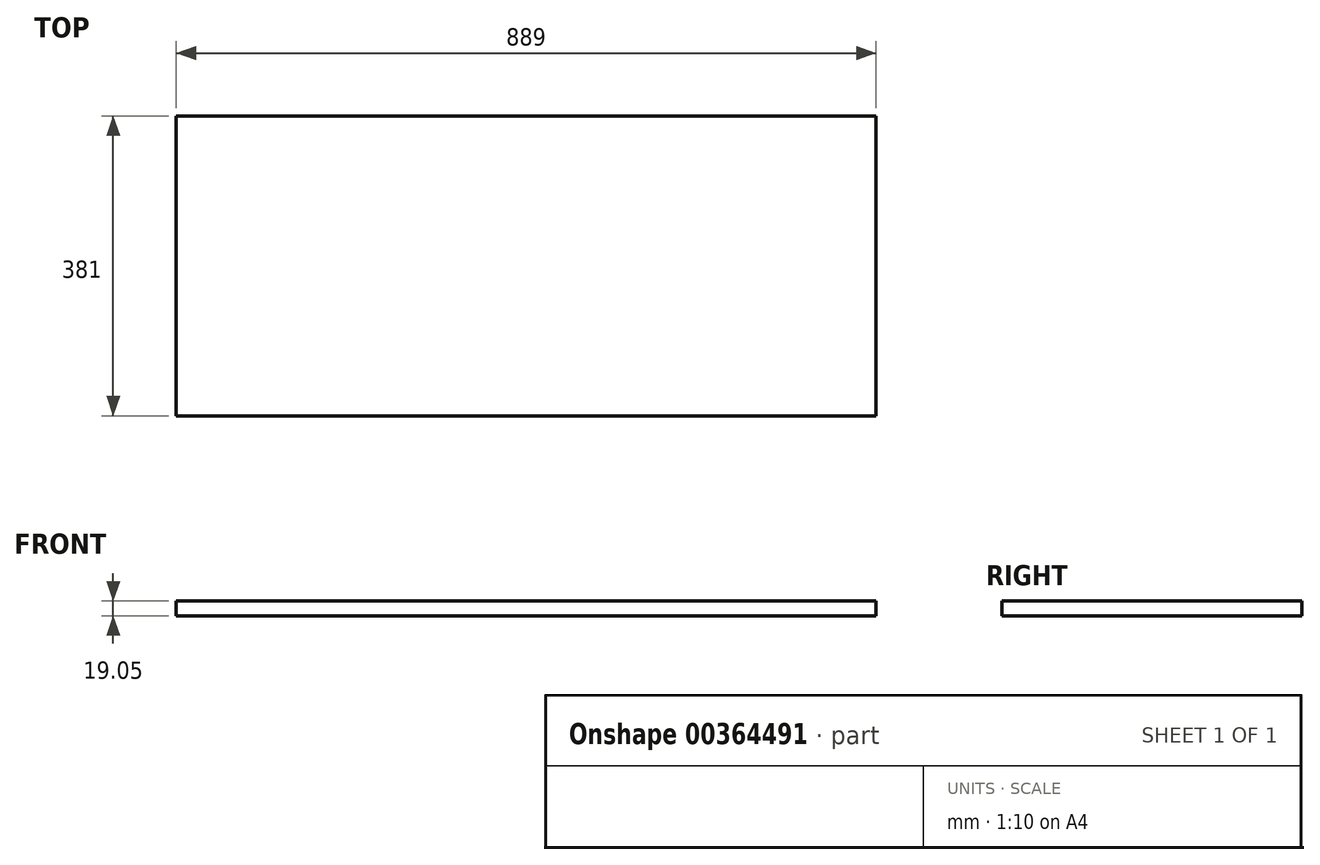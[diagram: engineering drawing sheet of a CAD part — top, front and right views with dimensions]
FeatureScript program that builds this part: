
annotation { "Feature Type Name" : "Feature", "Feature Type Description" : "" }
export const myFeature = defineFeature(function(context is Context, id is Id, definition is map)
    precondition{}
    {
        {
            var Q0;
            Q0=qCreatedBy(makeId("Top.planeOp"),FACE);
            var sketch = newSketch(context, id + "F0", { "sketchPlane" : qUnion([Q0])});
            skLineSegment(sketch, "E0.bottom", {"start": v(0, 0) * mm, "end": v(889, 0) * mm});
            skLineSegment(sketch, "E0.top", {"start": v(0, 381) * mm, "end": v(889, 381) * mm});
            skLineSegment(sketch, "E0.left", {"start": v(0, 0) * mm, "end": v(0, 381) * mm});
            skLineSegment(sketch, "E0.right", {"start": v(889, 0) * mm, "end": v(889, 381) * mm});
            skSolve(sketch);
        }
        {
            var Q0;
            Q0 = qSketchRegion(id + "F0", true);
            extrude(context, id + "F1", {"entities" : qUnion([Q0]), "depth" : 19.05 * mm});
        }
    });
